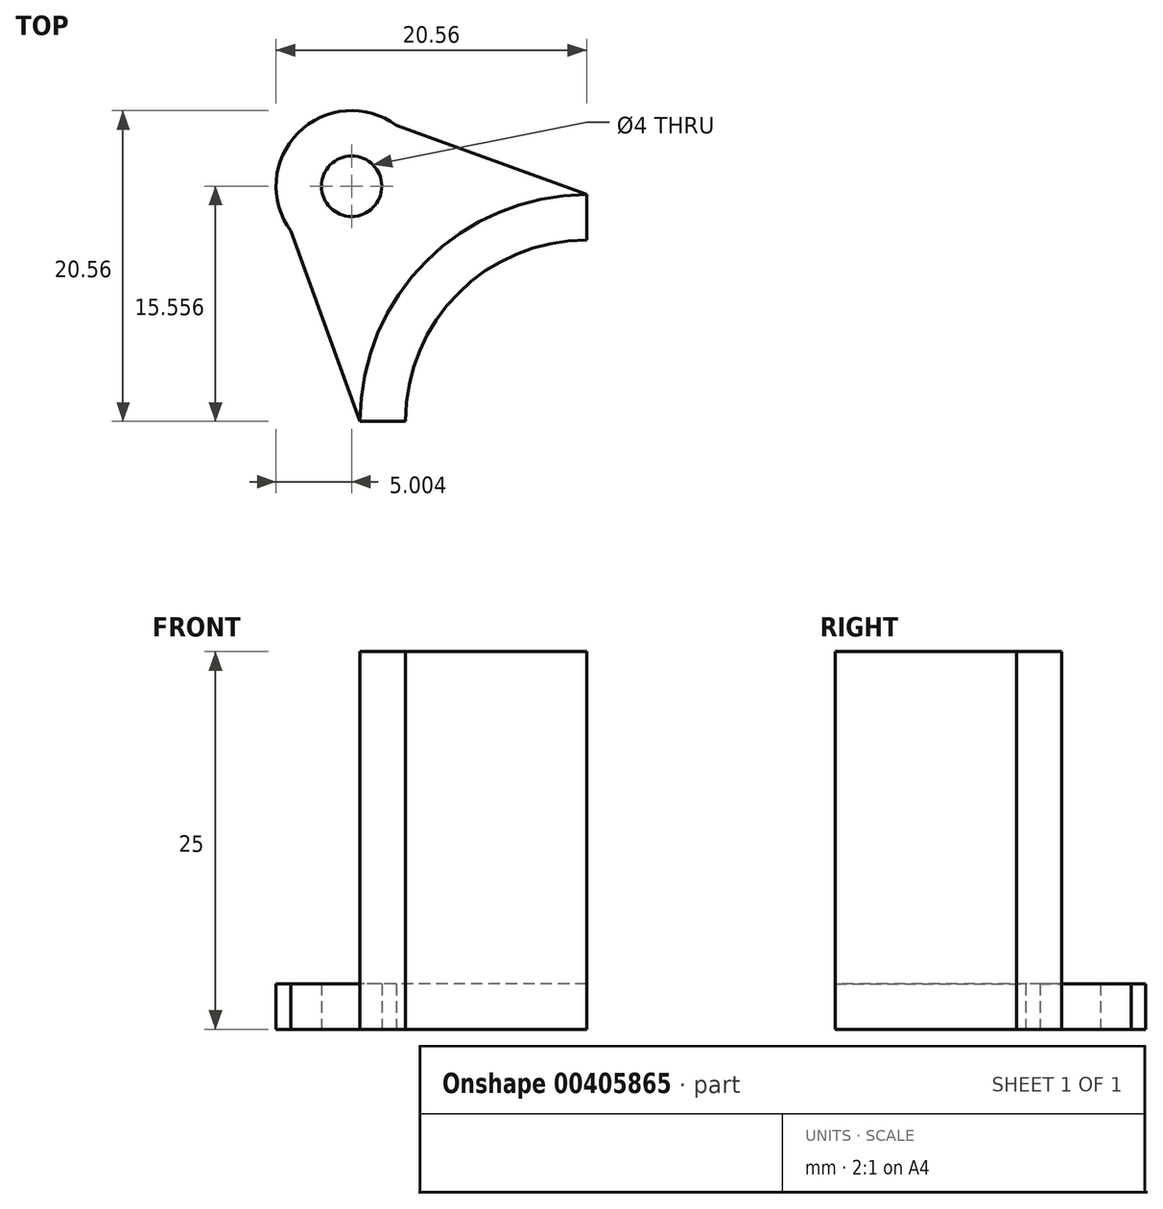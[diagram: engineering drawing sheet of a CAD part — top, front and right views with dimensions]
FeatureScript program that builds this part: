
annotation { "Feature Type Name" : "Feature", "Feature Type Description" : "" }
export const myFeature = defineFeature(function(context is Context, id is Id, definition is map)
    precondition{}
    {
        {
            var Q0;
            Q0=qCreatedBy(makeId("Top.planeOp"),FACE);
            var sketch = newSketch(context, id + "F0", { "sketchPlane" : qUnion([Q0])});
            skCircle(sketch, "E0", {"center": v(-15.56, 15.56) * mm, "radius": 2 * mm});
            skLineSegment(sketch, "E1", {"start": v(0, 0) * mm, "end": v(0, 28.56) * mm, "construction": true});
            skLineSegment(sketch, "E2", {"start": v(0, 0) * mm, "end": v(-26.2, 0) * mm, "construction": true});
            skArc(sketch, "E3", {"start": v(0, 12) * mm, "mid": v(-8.49, 8.49) * mm, "end": v(-12, 0) * mm});
            skLineSegment(sketch, "E4", {"start": v(0, 0) * mm, "end": v(-15.56, 15.56) * mm});
            skArc(sketch, "E5", {"start": v(0, 15) * mm, "mid": v(-10.6, 10.6) * mm, "end": v(-15, 0) * mm});
            skLineSegment(sketch, "E6", {"start": v(0, 15) * mm, "end": v(0, 12) * mm});
            skLineSegment(sketch, "E7", {"start": v(-15, 0) * mm, "end": v(-12, 0) * mm});
            skLineSegment(sketch, "E8", {"start": v(-15, 0) * mm, "end": v(-19.58, 12.6) * mm});
            skLineSegment(sketch, "E9", {"start": v(0, 15) * mm, "end": v(-12.6, 19.58) * mm});
            skArc(sketch, "E10", {"start": v(-12.6, 19.58) * mm, "mid": v(-19.1, 19.1) * mm, "end": v(-19.58, 12.6) * mm});
            skSolve(sketch);
        }
        {
            var Q0;
            Q0=makeQuery(id+"F0.imprint","IMPRINT",FACE,{"disambiguationData":[TD([[makeQuery(id+"F0.imprint","IMPRINT",EDGE,{"derivedFrom":sQuery(id+"F0.wireOp",EDGE,"E0")}),-1.0]])]});
            extrude(context, id + "F1", {"entities" : qUnion([Q0]), "depth" : 3 * mm});
        }
        {
            var Q0;
            {var subQ0=sQuery(id+"F0.wireOp",EDGE,"E7");Q0=makeQuery(id+"F0.imprint","IMPRINT",FACE,{"disambiguationData":[TD([[makeQuery(id+"F0.imprint","IMPRINT",EDGE,{"derivedFrom":subQ0}),1.0]])]});}
            var Q1;
            {var subQ0=sQuery(id+"F0.wireOp",EDGE,"E6");Q1=makeQuery(id+"F0.imprint","IMPRINT",FACE,{"disambiguationData":[TD([[makeQuery(id+"F0.imprint","IMPRINT",EDGE,{"derivedFrom":subQ0}),-1.0]])]});}
            extrude(context, id + "F2", {"entities" : qUnion([Q0, Q1]), "operationType" : NewBodyOperationType.ADD, "depth" : 25 * mm});
        }
    });
